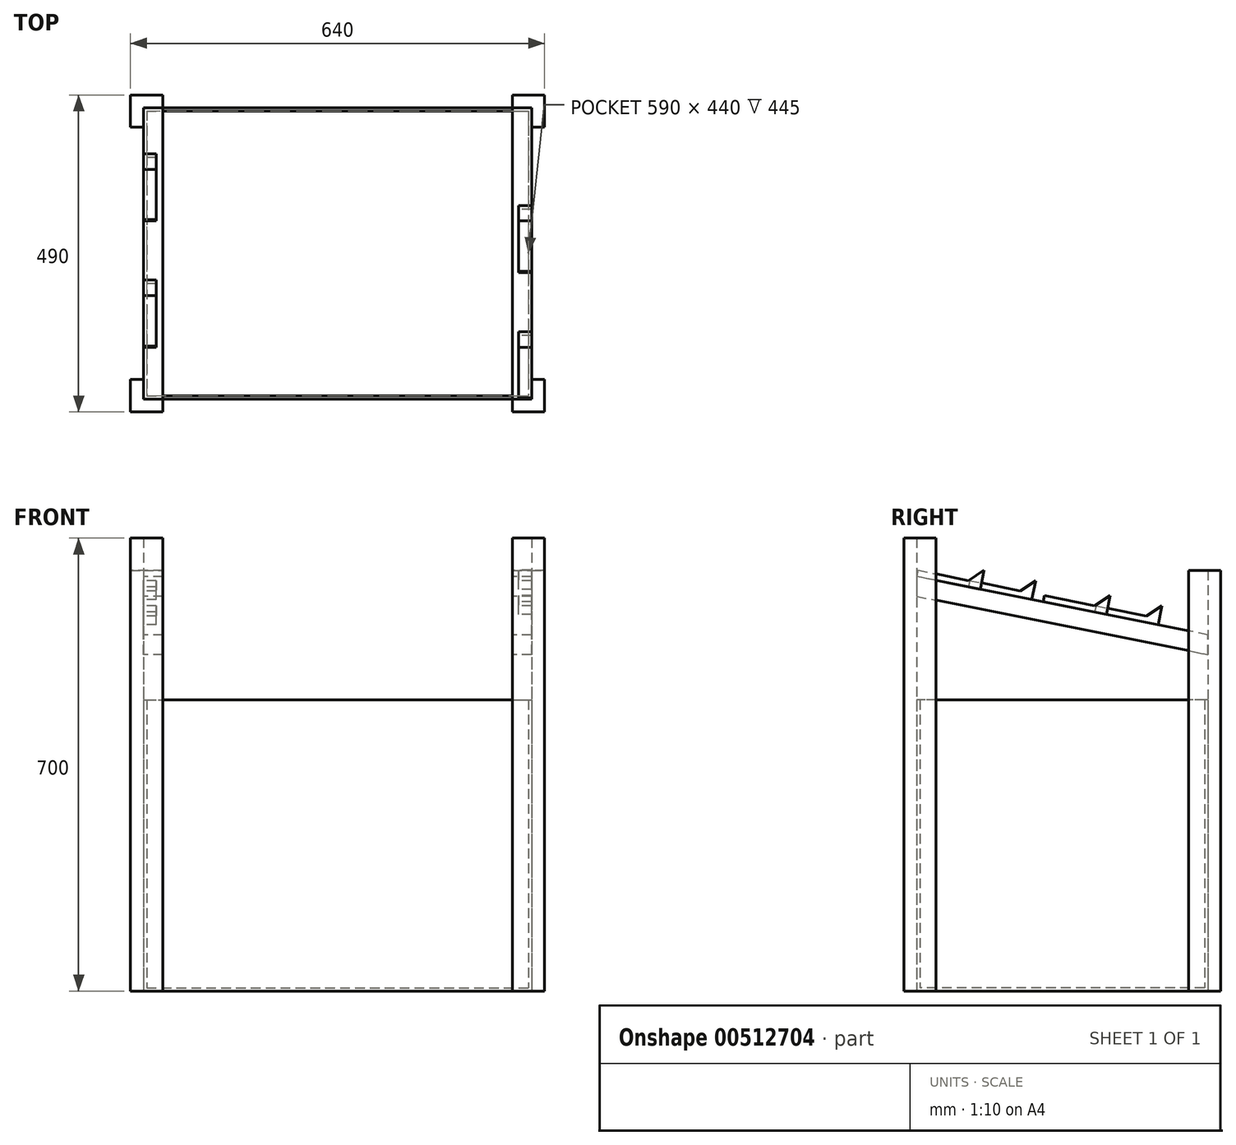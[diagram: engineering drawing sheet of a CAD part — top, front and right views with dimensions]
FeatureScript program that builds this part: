
annotation { "Feature Type Name" : "Feature", "Feature Type Description" : "" }
export const myFeature = defineFeature(function(context is Context, id is Id, definition is map)
    precondition{}
    {
        {
            var Q0;
            Q0=qCreatedBy(makeId("Top.planeOp"),FACE);
            var sketch = newSketch(context, id + "F0", { "sketchPlane" : qUnion([Q0])});
            skLineSegment(sketch, "E0.bottom", {"start": v(-300, 225) * mm, "end": v(300, 225) * mm});
            skLineSegment(sketch, "E0.top", {"start": v(-300, -225) * mm, "end": v(300, -225) * mm});
            skLineSegment(sketch, "E0.left", {"start": v(-300, 225) * mm, "end": v(-300, -225) * mm});
            skLineSegment(sketch, "E0.right", {"start": v(300, 225) * mm, "end": v(300, -225) * mm});
            skPoint(sketch, "E0.middle", {"position": v(0, 0) * mm});
            skSolve(sketch);
        }
        {
            var Q0;
            Q0=qSketchRegion(id+"F0",true);
            extrude(context, id + "F1", {"entities" : qUnion([Q0]), "depth" : 450 * mm});
        }
        {
            var Q0;
            Q0=makeQuery(id+"F1.opExtrude","CAP_FACE",FACE,{"disambiguationData":[OSD([sQuery(id+"F0.wireOp",EDGE,"E0.bottom"),sQuery(id+"F0.wireOp",EDGE,"E0.top"),sQuery(id+"F0.wireOp",EDGE,"E0.left"),sQuery(id+"F0.wireOp",EDGE,"E0.right")])],"isStart":false});
            shell(context, id + "F2", {"entities" : qUnion([Q0]), "thickness" : 5 * mm});
        }
        {
            var Q0;
            Q0=makeQuery(id+"F1.opExtrude","CAP_FACE",FACE,{"disambiguationData":[OSD([sQuery(id+"F0.wireOp",EDGE,"E0.bottom"),sQuery(id+"F0.wireOp",EDGE,"E0.top"),sQuery(id+"F0.wireOp",EDGE,"E0.left"),sQuery(id+"F0.wireOp",EDGE,"E0.right")])],"isStart":true});
            var sketch = newSketch(context, id + "F3", { "sketchPlane" : qUnion([Q0])});
            skLineSegment(sketch, "E1", {"start": v(-300, 195) * mm, "end": v(-320, 195) * mm});
            skLineSegment(sketch, "E2", {"start": v(-320, 195) * mm, "end": v(-320, 245) * mm});
            skLineSegment(sketch, "E3", {"start": v(-320, 245) * mm, "end": v(-270, 245) * mm});
            skLineSegment(sketch, "E4", {"start": v(-270, 245) * mm, "end": v(-270, 225) * mm});
            skLineSegment(sketch, "E5", {"start": v(-270, 225) * mm, "end": v(-300, 225) * mm});
            skLineSegment(sketch, "E6", {"start": v(-300, 225) * mm, "end": v(-300, 195) * mm});
            skSolve(sketch);
        }
        {
            var Q0;
            Q0=qSketchRegion(id+"F3",true);
            extrude(context, id + "F4", {"entities" : qUnion([Q0]), "oppositeDirection" : true, "depth" : 700 * mm});
        }
        {
            var Q0;
            Q0=makeQuery(id+"F4.opExtrude","SWEPT_BODY",BODY,{"disambiguationData":[OSD([sQuery(id+"F3.wireOp",EDGE,"E1"),sQuery(id+"F3.wireOp",EDGE,"E2"),sQuery(id+"F3.wireOp",EDGE,"E3"),sQuery(id+"F3.wireOp",EDGE,"E4"),sQuery(id+"F3.wireOp",EDGE,"E5"),sQuery(id+"F3.wireOp",EDGE,"E6")])]});
            transform(context, id + "F5", {"entities" : qUnion([Q0]), "transformType" : TransformType.TRANSLATION_3D, "dx" : 600 * mm, "dy" : 0 * mm, "dz" : 0 * mm, "makeCopy" : true});
        }
        {
            var Q0;
            Q0=makeQuery(id+"F5.opPattern","COPY",BODY,{"derivedFrom":makeQuery(id+"F4.opExtrude","SWEPT_BODY",BODY,{"disambiguationData":[OSD([sQuery(id+"F3.wireOp",EDGE,"E1"),sQuery(id+"F3.wireOp",EDGE,"E2"),sQuery(id+"F3.wireOp",EDGE,"E3"),sQuery(id+"F3.wireOp",EDGE,"E4"),sQuery(id+"F3.wireOp",EDGE,"E5"),sQuery(id+"F3.wireOp",EDGE,"E6")])]}),"instanceName":"1"});
            var Q1;
            Q1=makeQuery(id+"F1.opExtrude","SWEPT_EDGE",EDGE,{"disambiguationData":[OSD([sQuery(id+"F0.wireOp",EDGE,"E0.top"),sQuery(id+"F0.wireOp",EDGE,"E0.right")])]});
            transform(context, id + "F6", {"entities" : qUnion([Q0]), "transformType" : TransformType.ROTATION, "transformAxis" : qUnion([Q1]), "angle" : 90 * degree, "oppositeDirection" : true, "makeCopy" : false});
        }
        {
            var Q0;
            Q0=makeQuery(id+"F1.opExtrude","CAP_FACE",FACE,{"disambiguationData":[OSD([sQuery(id+"F0.wireOp",EDGE,"E0.bottom"),sQuery(id+"F0.wireOp",EDGE,"E0.top"),sQuery(id+"F0.wireOp",EDGE,"E0.left"),sQuery(id+"F0.wireOp",EDGE,"E0.right")])],"isStart":true});
            var sketch = newSketch(context, id + "F7", { "sketchPlane" : qUnion([Q0])});
            skLineSegment(sketch, "E7", {"start": v(300, -195) * mm, "end": v(320, -195) * mm});
            skLineSegment(sketch, "E8", {"start": v(320, -195) * mm, "end": v(320, -245) * mm});
            skLineSegment(sketch, "E9", {"start": v(320, -245) * mm, "end": v(270, -245) * mm});
            skLineSegment(sketch, "E10", {"start": v(270, -245) * mm, "end": v(270, -225) * mm});
            skLineSegment(sketch, "E11", {"start": v(270, -225) * mm, "end": v(300, -225) * mm});
            skLineSegment(sketch, "E12", {"start": v(300, -225) * mm, "end": v(300, -195) * mm});
            skSolve(sketch);
        }
        {
            var Q0;
            Q0=qSketchRegion(id+"F7",true);
            extrude(context, id + "F8", {"entities" : qUnion([Q0]), "oppositeDirection" : true, "depth" : 650 * mm});
        }
        {
            var Q0;
            Q0=makeQuery(id+"F8.opExtrude","SWEPT_BODY",BODY,{"disambiguationData":[OSD([sQuery(id+"F7.wireOp",EDGE,"E7"),sQuery(id+"F7.wireOp",EDGE,"E8"),sQuery(id+"F7.wireOp",EDGE,"E9"),sQuery(id+"F7.wireOp",EDGE,"E10"),sQuery(id+"F7.wireOp",EDGE,"E11"),sQuery(id+"F7.wireOp",EDGE,"E12")])]});
            transform(context, id + "F9", {"entities" : qUnion([Q0]), "transformType" : TransformType.TRANSLATION_3D, "dx" : -600 * mm, "dy" : 0 * mm, "dz" : 0 * mm, "makeCopy" : true});
        }
        {
            var Q0;
            Q0=makeQuery(id+"F9.opPattern","COPY",BODY,{"derivedFrom":makeQuery(id+"F8.opExtrude","SWEPT_BODY",BODY,{"disambiguationData":[OSD([sQuery(id+"F7.wireOp",EDGE,"E7"),sQuery(id+"F7.wireOp",EDGE,"E8"),sQuery(id+"F7.wireOp",EDGE,"E9"),sQuery(id+"F7.wireOp",EDGE,"E10"),sQuery(id+"F7.wireOp",EDGE,"E11"),sQuery(id+"F7.wireOp",EDGE,"E12")])]}),"instanceName":"1"});
            var Q1;
            Q1=makeQuery(id+"F1.opExtrude","SWEPT_EDGE",EDGE,{"disambiguationData":[OSD([sQuery(id+"F0.wireOp",EDGE,"E0.bottom"),sQuery(id+"F0.wireOp",EDGE,"E0.left")])]});
            transform(context, id + "F10", {"entities" : qUnion([Q0]), "transformType" : TransformType.ROTATION, "transformAxis" : qUnion([Q1]), "angle" : 90 * degree, "oppositeDirection" : true, "makeCopy" : false});
        }
        {
            var Q0;
            Q0=makeQuery(id+"F1.opExtrude","SWEPT_FACE",FACE,{"disambiguationData":[OSD([sQuery(id+"F0.wireOp",EDGE,"E0.left")])]});
            var sketch = newSketch(context, id + "F11", { "sketchPlane" : qUnion([Q0])});
            skLineSegment(sketch, "E13", {"start": v(-225, 520) * mm, "end": v(-225, 550.6) * mm});
            skLineSegment(sketch, "E14", {"start": v(-225, 550.6) * mm, "end": v(225, 640.6) * mm});
            skLineSegment(sketch, "E15", {"start": v(225, 640.6) * mm, "end": v(225, 610) * mm});
            skLineSegment(sketch, "E16", {"start": v(225, 610) * mm, "end": v(-225, 520) * mm});
            skSolve(sketch);
        }
        {
            var Q0;
            Q0 = qSketchRegion(id + "F11", true);
            extrude(context, id + "F12", {"entities" : qUnion([Q0]), "oppositeDirection" : true, "depth" : 30 * mm});
        }
        {
            var Q0;
            Q0=makeQuery(id+"F12.opExtrude","SWEPT_BODY",BODY,{"disambiguationData":[OSD([sQuery(id+"F11.wireOp",EDGE,"E13"),sQuery(id+"F11.wireOp",EDGE,"E14"),sQuery(id+"F11.wireOp",EDGE,"E15"),sQuery(id+"F11.wireOp",EDGE,"E16")])]});
            transform(context, id + "F13", {"entities" : qUnion([Q0]), "transformType" : TransformType.TRANSLATION_3D, "dx" : 570 * mm, "dy" : 0 * mm, "dz" : 0 * mm, "makeCopy" : true});
        }
        {
            var Q0;
            Q0=makeQuery(id+"F12.opExtrude","CAP_FACE",FACE,{"disambiguationData":[OSD([sQuery(id+"F11.wireOp",EDGE,"E13"),sQuery(id+"F11.wireOp",EDGE,"E14"),sQuery(id+"F11.wireOp",EDGE,"E15"),sQuery(id+"F11.wireOp",EDGE,"E16")])],"isStart":true});
            var sketch = newSketch(context, id + "F14", { "sketchPlane" : qUnion([Q0])});
            skCircle(sketch, "E17", {"center": v(175, 681.58) * mm, "radius": 50 * mm, "construction": true});
            skCircle(sketch, "E18", {"center": v(-20.19, 642.55) * mm, "radius": 50 * mm, "construction": true});
            skCircle(sketch, "E19", {"center": v(75.5, 671.58) * mm, "radius": 50 * mm, "construction": true});
            skCircle(sketch, "E20", {"center": v(-119.69, 632.55) * mm, "radius": 50 * mm, "construction": true});
            skLineSegment(sketch, "E21", {"start": v(75.5, 671.58) * mm, "end": v(175, 681.58) * mm, "construction": true});
            skLineSegment(sketch, "E22", {"start": v(-119.69, 632.55) * mm, "end": v(-20.19, 642.55) * mm, "construction": true});
            skLineSegment(sketch, "E23", {"start": v(-148.19, 565.96) * mm, "end": v(-154.07, 595.37) * mm});
            skLineSegment(sketch, "E24", {"start": v(-52.14, 595.36) * mm, "end": v(-50.13, 585.57) * mm});
            skLineSegment(sketch, "E25", {"start": v(-50.13, 585.57) * mm, "end": v(-148.19, 565.96) * mm});
            skLineSegment(sketch, "E26", {"start": v(-52.14, 595.36) * mm, "end": v(-130.07, 579.37) * mm});
            skLineSegment(sketch, "E27", {"start": v(-130.07, 579.37) * mm, "end": v(-154.07, 595.37) * mm});
            skLineSegment(sketch, "E28", {"start": v(47, 605) * mm, "end": v(41.12, 634.41) * mm});
            skLineSegment(sketch, "E29", {"start": v(143.05, 634.4) * mm, "end": v(145.06, 624.6) * mm});
            skLineSegment(sketch, "E30", {"start": v(145.06, 624.6) * mm, "end": v(47, 605) * mm});
            skLineSegment(sketch, "E31", {"start": v(143.05, 634.4) * mm, "end": v(65.12, 618.41) * mm});
            skLineSegment(sketch, "E32", {"start": v(65.12, 618.41) * mm, "end": v(41.12, 634.41) * mm});
            skSolve(sketch);
        }
        {
            var Q0;
            Q0 = qSketchRegion(id + "F14", true);
            extrude(context, id + "F15", {"entities" : qUnion([Q0]), "oppositeDirection" : true, "depth" : 20 * mm});
        }
        {
            var Q0;
            Q0=makeQuery(id+"F15.opExtrude","SWEPT_BODY",BODY,{"disambiguationData":[OSD([sQuery(id+"F14.wireOp",EDGE,"E28"),sQuery(id+"F14.wireOp",EDGE,"E29"),sQuery(id+"F14.wireOp",EDGE,"E30"),sQuery(id+"F14.wireOp",EDGE,"E31"),sQuery(id+"F14.wireOp",EDGE,"E32")])]});
            transform(context, id + "F16", {"entities" : qUnion([Q0]), "transformType" : TransformType.TRANSLATION_3D, "dx" : 580 * mm, "dy" : 0 * mm, "dz" : 0 * mm, "makeCopy" : true});
        }
        {
            var Q0;
            Q0=makeQuery(id+"F15.opExtrude","SWEPT_BODY",BODY,{"disambiguationData":[OSD([sQuery(id+"F14.wireOp",EDGE,"E23"),sQuery(id+"F14.wireOp",EDGE,"E24"),sQuery(id+"F14.wireOp",EDGE,"E25"),sQuery(id+"F14.wireOp",EDGE,"E26"),sQuery(id+"F14.wireOp",EDGE,"E27")])]});
            transform(context, id + "F17", {"entities" : qUnion([Q0]), "transformType" : TransformType.TRANSLATION_3D, "dx" : 580 * mm, "dy" : 0 * mm, "dz" : 0 * mm, "makeCopy" : true});
        }
        {
            var Q0;
            Q0=makeQuery(id+"F16.opPattern","COPY",BODY,{"derivedFrom":makeQuery(id+"F15.opExtrude","SWEPT_BODY",BODY,{"disambiguationData":[OSD([sQuery(id+"F14.wireOp",EDGE,"E28"),sQuery(id+"F14.wireOp",EDGE,"E29"),sQuery(id+"F14.wireOp",EDGE,"E30"),sQuery(id+"F14.wireOp",EDGE,"E31"),sQuery(id+"F14.wireOp",EDGE,"E32")])]}),"instanceName":"1"});
            var Q1;
            Q1=makeQuery(id+"F17.opPattern","COPY",BODY,{"derivedFrom":makeQuery(id+"F15.opExtrude","SWEPT_BODY",BODY,{"disambiguationData":[OSD([sQuery(id+"F14.wireOp",EDGE,"E23"),sQuery(id+"F14.wireOp",EDGE,"E24"),sQuery(id+"F14.wireOp",EDGE,"E25"),sQuery(id+"F14.wireOp",EDGE,"E26"),sQuery(id+"F14.wireOp",EDGE,"E27")])]}),"instanceName":"1"});
            var Q2;
            Q2=makeQuery(id+"F16.opPattern","COPY",VERTEX,{"derivedFrom":makeQuery(id+"F15.opExtrude","CAP_VERTEX",VERTEX,{"disambiguationData":[OSD([sQuery(id+"F11.wireOp",EDGE,"E14"),sQuery(id+"F14.wireOp",EDGE,"E29"),sQuery(id+"F14.wireOp",EDGE,"E30")])],"isStart":false}),"instanceName":"1"});
            var Q3;
            Q3=makeQuery(id+"F13.opPattern","COPY",VERTEX,{"derivedFrom":makeQuery(id+"F12.opExtrude","CAP_VERTEX",VERTEX,{"disambiguationData":[OSD([sQuery(id+"F11.wireOp",EDGE,"E14"),sQuery(id+"F11.wireOp",EDGE,"E15")])],"isStart":false}),"instanceName":"1"});
            transform(context, id + "F18", {"entities" : qUnion([Q0, Q1]), "transformType" : TransformType.TRANSLATION_ENTITY, "oppositeDirectionEntity" : false, "transformLine" : qUnion([Q2, Q3]), "makeCopy" : false});
        }
    });
